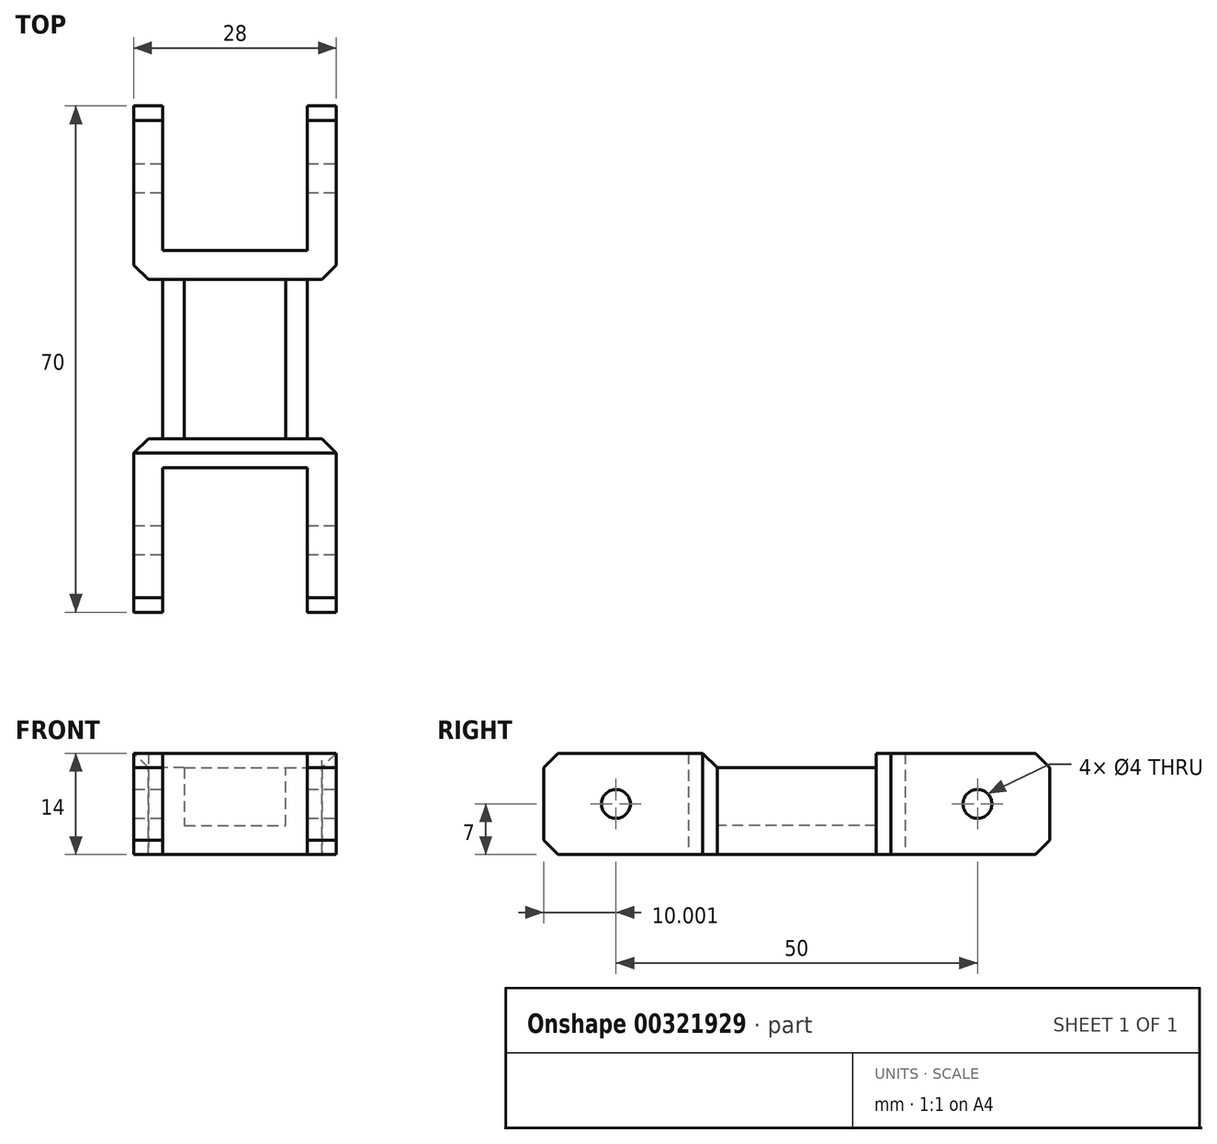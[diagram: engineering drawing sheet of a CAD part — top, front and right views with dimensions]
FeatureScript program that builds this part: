
annotation { "Feature Type Name" : "Feature", "Feature Type Description" : "" }
export const myFeature = defineFeature(function(context is Context, id is Id, definition is map)
    precondition{}
    {
        {
            var Q0;
            Q0=qCreatedBy(makeId("Top.planeOp"),FACE);
            var sketch = newSketch(context, id + "F0", { "sketchPlane" : qUnion([Q0])});
            skLineSegment(sketch, "E0.bottom", {"start": v(-54.4, 33.69) * mm, "end": v(-34.4, 33.69) * mm});
            skLineSegment(sketch, "E0.top", {"start": v(-54.4, 13.29) * mm, "end": v(-34.4, 13.29) * mm});
            skLineSegment(sketch, "E0.left", {"start": v(-54.4, 33.69) * mm, "end": v(-54.4, 13.29) * mm});
            skLineSegment(sketch, "E0.right", {"start": v(-34.4, 33.69) * mm, "end": v(-34.4, 13.29) * mm});
            skLineSegment(sketch, "E1.bottom", {"start": v(-54.4, 63.69) * mm, "end": v(-34.4, 63.69) * mm});
            skLineSegment(sketch, "E1.top", {"start": v(-54.4, 9.29) * mm, "end": v(-34.4, 9.29) * mm});
            skLineSegment(sketch, "E1.left", {"start": v(-54.4, 63.69) * mm, "end": v(-54.4, 9.29) * mm});
            skLineSegment(sketch, "E1.right", {"start": v(-34.4, 63.69) * mm, "end": v(-34.4, 9.29) * mm});
            skLineSegment(sketch, "E2", {"start": v(-54.4, 59.69) * mm, "end": v(-34.4, 59.69) * mm});
            skLineSegment(sketch, "E3", {"start": v(-54.4, 37.69) * mm, "end": v(-34.4, 37.69) * mm});
            skSolve(sketch);
        }
        {
            var Q0;
            {var subQ0=sQuery(id+"F0.wireOp",EDGE,"E2");Q0=makeQuery(id+"F0.imprint","IMPRINT",FACE,{"disambiguationData":[TD([[makeQuery(id+"F0.imprint","IMPRINT",EDGE,{"derivedFrom":subQ0}),-1.0]])]});}
            var Q1;
            {var subQ0=sQuery(id+"F0.wireOp",EDGE,"E1.bottom");Q1=makeQuery(id+"F0.imprint","IMPRINT",FACE,{"disambiguationData":[TD([[makeQuery(id+"F0.imprint","IMPRINT",EDGE,{"derivedFrom":subQ0}),-1.0]])]});}
            var Q2;
            Q2=makeQuery(id+"F0.imprint","IMPRINT",FACE,{"disambiguationData":[TD([[makeQuery(id+"F0.imprint","IMPRINT",EDGE,{"derivedFrom":sQuery(id+"F0.wireOp",EDGE,"E0.bottom")}),1.0]])]});
            var Q3;
            {var subQ0=sQuery(id+"F0.wireOp",EDGE,"E0.bottom");Q3=makeQuery(id+"F0.imprint","IMPRINT",FACE,{"disambiguationData":[TD([[makeQuery(id+"F0.imprint","IMPRINT",EDGE,{"derivedFrom":subQ0}),-1.0]])]});}
            var Q4;
            {var subQ0=sQuery(id+"F0.wireOp",EDGE,"E0.top");Q4=makeQuery(id+"F0.imprint","IMPRINT",FACE,{"disambiguationData":[TD([[makeQuery(id+"F0.imprint","IMPRINT",EDGE,{"derivedFrom":subQ0}),-1.0]])]});}
            extrude(context, id + "F1", {"entities" : qUnion([Q0, Q1, Q2, Q3, Q4]), "oppositeDirection" : true, "depth" : 2 * mm});
        }
        {
            var Q0;
            Q0=makeQuery(id+"F0.imprint","IMPRINT",FACE,{"disambiguationData":[TD([[makeQuery(id+"F0.imprint","IMPRINT",EDGE,{"derivedFrom":sQuery(id+"F0.wireOp",EDGE,"E0.bottom")}),1.0]])]});
            var Q1;
            {var subQ0=sQuery(id+"F0.wireOp",EDGE,"E1.bottom");Q1=makeQuery(id+"F0.imprint","IMPRINT",FACE,{"disambiguationData":[TD([[makeQuery(id+"F0.imprint","IMPRINT",EDGE,{"derivedFrom":subQ0}),-1.0]])]});}
            var Q2;
            {var subQ0=sQuery(id+"F0.wireOp",EDGE,"E0.top");Q2=makeQuery(id+"F0.imprint","IMPRINT",FACE,{"disambiguationData":[TD([[makeQuery(id+"F0.imprint","IMPRINT",EDGE,{"derivedFrom":subQ0}),-1.0]])]});}
            extrude(context, id + "F2", {"entities" : qUnion([Q0, Q1, Q2]), "operationType" : NewBodyOperationType.ADD, "depth" : 10 * mm});
        }
        {
            var Q0;
            {var subQ0=sQuery(id+"F0.wireOp",EDGE,"E1.top");Q0=makeQuery(id+"F2.boolean.opBoolean","MERGE",FACE,{"derivedFrom":[makeQuery(id+"F1.opExtrude","SWEPT_FACE",FACE,{"disambiguationData":[OSD([subQ0])]}),makeQuery(id+"F2.opExtrude","SWEPT_FACE",FACE,{"disambiguationData":[OSD([subQ0])]})]});}
            var sketch = newSketch(context, id + "F3", { "sketchPlane" : qUnion([Q0])});
            skCircle(sketch, "E4", {"center": v(-44.4, 5.5) * mm, "radius": 2.2 * mm});
            skPoint(sketch, "E4.centerSnap0", {"position": v(-44.4, -2) * mm});
            skSolve(sketch);
        }
        {
            var Q0;
            Q0=makeQuery(id+"F3.imprint","IMPRINT",FACE,{"disambiguationData":[TD([[makeQuery(id+"F3.imprint","IMPRINT",EDGE,{"derivedFrom":sQuery(id+"F3.wireOp",EDGE,"E4")}),1.0]])]});
            extrude(context, id + "F4", {"entities" : qUnion([Q0]), "operationType" : NewBodyOperationType.REMOVE, "oppositeDirection" : true, "depth" : 30 * mm, "offsetDistance" : 25 * mm});
        }
        {
            var Q0;
            {var subQ0=sQuery(id+"F0.wireOp",EDGE,"E1.left");Q0=makeQuery(id+"F2.boolean.opBoolean","MERGE",FACE,{"derivedFrom":[makeQuery(id+"F1.opExtrude","SWEPT_FACE",FACE,{"disambiguationData":[OSD([subQ0])]}),makeQuery(id+"F2.opExtrude","SWEPT_FACE",FACE,{"disambiguationData":[OSD([subQ0]),TDD([makeQuery(id+"F0.imprint","IMPRINT",EDGE,{"disambiguationData":[TD([[makeQuery(id+"F0.imprint","INTERSECT",VERTEX,{"derivedFrom":[sQuery(id+"F0.wireOp",EDGE,"E1.bottom"),subQ0]}),-1.0]])],"derivedFrom":subQ0})])]}),makeQuery(id+"F2.opExtrude","SWEPT_FACE",FACE,{"disambiguationData":[OSD([subQ0]),TDD([makeQuery(id+"F0.imprint","IMPRINT",EDGE,{"disambiguationData":[TD([[makeQuery(id+"F0.imprint","INTERSECT",VERTEX,{"derivedFrom":[sQuery(id+"F0.wireOp",EDGE,"E0.bottom"),subQ0]}),1.0]])],"derivedFrom":subQ0})])]}),makeQuery(id+"F2.opExtrude","SWEPT_FACE",FACE,{"disambiguationData":[OSD([subQ0]),TDD([makeQuery(id+"F0.imprint","IMPRINT",EDGE,{"disambiguationData":[TD([[makeQuery(id+"F0.imprint","INTERSECT",VERTEX,{"derivedFrom":[sQuery(id+"F0.wireOp",EDGE,"E0.top"),subQ0]}),-1.0]])],"derivedFrom":subQ0})])]})]});}
            var sketch = newSketch(context, id + "F5", { "sketchPlane" : qUnion([Q0])});
            skLineSegment(sketch, "E5.bottom", {"start": v(-59.69, 10) * mm, "end": v(-83.69, 10) * mm});
            skLineSegment(sketch, "E5.top", {"start": v(-59.69, -2) * mm, "end": v(-83.69, -2) * mm});
            skLineSegment(sketch, "E5.left", {"start": v(-59.69, 10) * mm, "end": v(-59.69, -2) * mm});
            skLineSegment(sketch, "E5.right", {"start": v(-83.69, 10) * mm, "end": v(-83.69, -2) * mm});
            skCircle(sketch, "E6", {"center": v(-73.69, 4) * mm, "radius": 2.6 * mm});
            skPoint(sketch, "E6.centerSnap0", {"position": v(-83.69, 4) * mm});
            skSolve(sketch);
        }
        {
            var Q0;
            {var subQ0=sQuery(id+"F0.wireOp",EDGE,"E1.right");Q0=makeQuery(id+"F2.boolean.opBoolean","MERGE",FACE,{"derivedFrom":[makeQuery(id+"F1.opExtrude","SWEPT_FACE",FACE,{"disambiguationData":[OSD([subQ0])]}),makeQuery(id+"F2.opExtrude","SWEPT_FACE",FACE,{"disambiguationData":[OSD([subQ0]),TDD([makeQuery(id+"F0.imprint","IMPRINT",EDGE,{"disambiguationData":[TD([[makeQuery(id+"F0.imprint","INTERSECT",VERTEX,{"derivedFrom":[sQuery(id+"F0.wireOp",EDGE,"E1.bottom"),subQ0]}),-1.0]])],"derivedFrom":subQ0})])]}),makeQuery(id+"F2.opExtrude","SWEPT_FACE",FACE,{"disambiguationData":[OSD([subQ0]),TDD([makeQuery(id+"F0.imprint","IMPRINT",EDGE,{"disambiguationData":[TD([[makeQuery(id+"F0.imprint","INTERSECT",VERTEX,{"derivedFrom":[sQuery(id+"F0.wireOp",EDGE,"E0.bottom"),subQ0]}),1.0]])],"derivedFrom":subQ0})])]}),makeQuery(id+"F2.opExtrude","SWEPT_FACE",FACE,{"disambiguationData":[OSD([subQ0]),TDD([makeQuery(id+"F0.imprint","IMPRINT",EDGE,{"disambiguationData":[TD([[makeQuery(id+"F0.imprint","INTERSECT",VERTEX,{"derivedFrom":[sQuery(id+"F0.wireOp",EDGE,"E0.top"),subQ0]}),-1.0]])],"derivedFrom":subQ0})])]})]});}
            var sketch = newSketch(context, id + "F6", { "sketchPlane" : qUnion([Q0])});
            skLineSegment(sketch, "E7.bottom", {"start": v(59.69, 10) * mm, "end": v(83.69, 10) * mm});
            skLineSegment(sketch, "E7.top", {"start": v(59.69, -2) * mm, "end": v(83.69, -2) * mm});
            skLineSegment(sketch, "E7.left", {"start": v(59.69, 10) * mm, "end": v(59.69, -2) * mm});
            skLineSegment(sketch, "E7.right", {"start": v(83.69, 10) * mm, "end": v(83.69, -2) * mm});
            skCircle(sketch, "E8", {"center": v(73.69, 4) * mm, "radius": 2.6 * mm});
            skPoint(sketch, "E8.centerSnap0", {"position": v(83.69, 4) * mm});
            skSolve(sketch);
        }
        {
            var Q0;
            {var subQ4=sQuery(id+"F5.wireOp",EDGE,"E5.right");Q0=makeQuery(id+"F5.imprint","IMPRINT",FACE,{"disambiguationData":[TD([[makeQuery(id+"F5.imprint","IMPRINT",EDGE,{"derivedFrom":subQ4}),1.0]])]});}
            var Q1;
            {var subQ3=sQuery(id+"F0.wireOp",EDGE,"E1.left");var subQ5=sQuery(id+"F0.wireOp",EDGE,"E1.bottom");var subQ10=makeQuery(id+"F2.boolean.opBoolean","MERGE",EDGE,{"derivedFrom":[makeQuery(id+"F1.opExtrude","SWEPT_EDGE",EDGE,{"disambiguationData":[OSD([subQ5,subQ3])]}),makeQuery(id+"F2.opExtrude","SWEPT_EDGE",EDGE,{"disambiguationData":[OSD([subQ5,subQ3])]})]});Q1=makeQuery(id+"F5.imprint","IMPRINT",FACE,{"disambiguationData":[TD([[makeQuery(id+"F5.imprint","IMPRINT",EDGE,{"derivedFrom":subQ10}),-1.0]])]});}
            extrude(context, id + "F7", {"entities" : qUnion([Q0, Q1]), "operationType" : NewBodyOperationType.ADD, "depth" : 4 * mm});
        }
        {
            var Q0;
            {var subQ0=sQuery(id+"F5.wireOp",EDGE,"As3iJ9jp-MM02-xgW6-gQvA-6wpTA8jTOXIw.right");Q0=makeQuery(id+"F5.imprint","IMPRINT",FACE,{"disambiguationData":[TD([[makeQuery(id+"F5.imprint","IMPRINT",EDGE,{"derivedFrom":subQ0}),-1.0]])]});}
            var Q1;
            {var subQ5=sQuery(id+"F5.wireOp",EDGE,"D0sxENBk-QWaU-MoL9-KmcH-z9rnvNsLjtkH");Q1=makeQuery(id+"F5.imprint","IMPRINT",FACE,{"disambiguationData":[TD([[makeQuery(id+"F5.imprint","IMPRINT",EDGE,{"derivedFrom":subQ5}),-1.0]])]});}
            var Q2;
            {var subQ4=sQuery(id+"F6.wireOp",EDGE,"E7.right");Q2=makeQuery(id+"F6.imprint","IMPRINT",FACE,{"disambiguationData":[TD([[makeQuery(id+"F6.imprint","IMPRINT",EDGE,{"derivedFrom":subQ4}),-1.0]])]});}
            var Q3;
            {var subQ3=sQuery(id+"F0.wireOp",EDGE,"E1.right");var subQ4=sQuery(id+"F0.wireOp",EDGE,"E1.bottom");var subQ10=makeQuery(id+"F2.boolean.opBoolean","MERGE",EDGE,{"derivedFrom":[makeQuery(id+"F1.opExtrude","SWEPT_EDGE",EDGE,{"disambiguationData":[OSD([subQ4,subQ3])]}),makeQuery(id+"F2.opExtrude","SWEPT_EDGE",EDGE,{"disambiguationData":[OSD([subQ4,subQ3])]})]});Q3=makeQuery(id+"F6.imprint","IMPRINT",FACE,{"disambiguationData":[TD([[makeQuery(id+"F6.imprint","IMPRINT",EDGE,{"derivedFrom":subQ10}),1.0]])]});}
            extrude(context, id + "F8", {"entities" : qUnion([Q0, Q1, Q2, Q3]), "operationType" : NewBodyOperationType.ADD, "depth" : 4 * mm});
        }
        {
            var Q0;
            Q0=makeQuery(id+"F8.boolean.opBoolean","MERGE",FACE,{"derivedFrom":[makeQuery(id+"F7.boolean.opBoolean","MERGE",FACE,{"derivedFrom":[makeQuery(id+"F1.opExtrude","CAP_FACE",FACE,{"disambiguationData":[OSD([sQuery(id+"F0.wireOp",EDGE,"E1.bottom"),sQuery(id+"F0.wireOp",EDGE,"E1.top"),sQuery(id+"F0.wireOp",EDGE,"E1.left"),sQuery(id+"F0.wireOp",EDGE,"E1.right")])],"isStart":false}),makeQuery(id+"F7.opExtrude","SWEPT_FACE",FACE,{"disambiguationData":[OSD([sQuery(id+"F5.wireOp",EDGE,"E5.top")])]})]}),makeQuery(id+"F8.opExtrude","SWEPT_FACE",FACE,{"disambiguationData":[OSD([sQuery(id+"F6.wireOp",EDGE,"E7.top")])]})]});
            var Q1;
            Q1=makeQuery(id+"F8.boolean.opBoolean","MERGE",FACE,{"derivedFrom":[makeQuery(id+"F7.boolean.opBoolean","MERGE",FACE,{"derivedFrom":[makeQuery(id+"F2.opExtrude","CAP_FACE",FACE,{"disambiguationData":[OSD([sQuery(id+"F0.wireOp",EDGE,"E1.bottom"),sQuery(id+"F0.wireOp",EDGE,"E1.left"),sQuery(id+"F0.wireOp",EDGE,"E1.right"),sQuery(id+"F0.wireOp",EDGE,"E2")])],"isStart":false}),makeQuery(id+"F7.opExtrude","SWEPT_FACE",FACE,{"disambiguationData":[OSD([sQuery(id+"F5.wireOp",EDGE,"E5.bottom")])]})]}),makeQuery(id+"F8.opExtrude","SWEPT_FACE",FACE,{"disambiguationData":[OSD([sQuery(id+"F6.wireOp",EDGE,"E7.bottom")])]})]});
            var Q2;
            Q2=makeQuery(id+"F2.opExtrude","CAP_FACE",FACE,{"disambiguationData":[OSD([sQuery(id+"F0.wireOp",EDGE,"E0.bottom"),sQuery(id+"F0.wireOp",EDGE,"E1.left"),sQuery(id+"F0.wireOp",EDGE,"E1.right"),sQuery(id+"F0.wireOp",EDGE,"E3")])],"isStart":false});
            var Q3;
            Q3=makeQuery(id+"F2.opExtrude","CAP_FACE",FACE,{"disambiguationData":[OSD([sQuery(id+"F0.wireOp",EDGE,"E0.top"),sQuery(id+"F0.wireOp",EDGE,"E1.top"),sQuery(id+"F0.wireOp",EDGE,"E1.left"),sQuery(id+"F0.wireOp",EDGE,"E1.right")])],"isStart":false});
            var Q4;
            {var subQ0=sQuery(id+"F0.wireOp",EDGE,"E1.right");var subQ1=sQuery(id+"F0.wireOp",EDGE,"E1.top");Q4=makeQuery(id+"F2.boolean.opBoolean","MERGE",EDGE,{"derivedFrom":[makeQuery(id+"F1.opExtrude","SWEPT_EDGE",EDGE,{"disambiguationData":[OSD([subQ1,subQ0])]}),makeQuery(id+"F2.opExtrude","SWEPT_EDGE",EDGE,{"disambiguationData":[OSD([subQ1,subQ0])]})]});}
            var Q5;
            {var subQ0=sQuery(id+"F0.wireOp",EDGE,"E1.left");var subQ1=sQuery(id+"F0.wireOp",EDGE,"E1.top");Q5=makeQuery(id+"F2.boolean.opBoolean","MERGE",EDGE,{"derivedFrom":[makeQuery(id+"F1.opExtrude","SWEPT_EDGE",EDGE,{"disambiguationData":[OSD([subQ1,subQ0])]}),makeQuery(id+"F2.opExtrude","SWEPT_EDGE",EDGE,{"disambiguationData":[OSD([subQ1,subQ0])]})]});}
            var Q6;
            Q6=makeQuery(id+"F7.opExtrude","CAP_EDGE",EDGE,{"disambiguationData":[OSD([sQuery(id+"F5.wireOp",EDGE,"E5.left")])],"isStart":false});
            var Q7;
            Q7=makeQuery(id+"F8.opExtrude","CAP_EDGE",EDGE,{"disambiguationData":[OSD([sQuery(id+"F6.wireOp",EDGE,"E7.left")])],"isStart":false});
            var Q8;
            Q8=makeQuery(id+"F8.opExtrude","CAP_EDGE",EDGE,{"disambiguationData":[OSD([sQuery(id+"F6.wireOp",EDGE,"E7.right")])],"isStart":false});
            var Q9;
            Q9=makeQuery(id+"F7.opExtrude","CAP_EDGE",EDGE,{"disambiguationData":[OSD([sQuery(id+"F5.wireOp",EDGE,"E5.right")])],"isStart":false});
            fillet(context, id + "F9", {"entities" : qUnion([Q0, Q1, Q2, Q3, Q4, Q5, Q6, Q7, Q8, Q9]), "radius" : 2 * mm, "allowEdgeOverflow" : false});
        }
        {
            var Q0;
            Q0=qCreatedBy(makeId("Top.planeOp"),FACE);
            var sketch = newSketch(context, id + "F10", { "sketchPlane" : qUnion([Q0])});
            skLineSegment(sketch, "E9.bottom", {"start": v(-54.07, -51.84) * mm, "end": v(-34.07, -51.84) * mm});
            skLineSegment(sketch, "E9.top", {"start": v(-54.07, -81.84) * mm, "end": v(-34.07, -81.84) * mm});
            skLineSegment(sketch, "E9.left", {"start": v(-54.07, -51.84) * mm, "end": v(-54.07, -81.84) * mm});
            skLineSegment(sketch, "E9.right", {"start": v(-34.07, -51.84) * mm, "end": v(-34.07, -81.84) * mm});
            skSolve(sketch);
        }
        {
            var Q0;
            Q0=qSketchRegion(id+"F10",true);
            extrude(context, id + "F11", {"entities" : qUnion([Q0]), "depth" : 4 * mm, "offsetDistance" : 25 * mm});
        }
        {
            var Q0;
            Q0=makeQuery(id+"F11.opExtrude","CAP_FACE",FACE,{"disambiguationData":[OSD([sQuery(id+"F10.wireOp",EDGE,"E9.bottom"),sQuery(id+"F10.wireOp",EDGE,"E9.top"),sQuery(id+"F10.wireOp",EDGE,"E9.left"),sQuery(id+"F10.wireOp",EDGE,"E9.right")])],"isStart":false});
            var sketch = newSketch(context, id + "F12", { "sketchPlane" : qUnion([Q0])});
            skLineSegment(sketch, "E10", {"start": v(-54.07, -55.84) * mm, "end": v(-34.07, -55.84) * mm});
            skLineSegment(sketch, "E11", {"start": v(-54.07, -77.84) * mm, "end": v(-34.07, -77.84) * mm});
            skSolve(sketch);
        }
        {
            var Q0;
            {var subQ0=sQuery(id+"F12.wireOp",EDGE,"E10");Q0=makeQuery(id+"F12.imprint","IMPRINT",FACE,{"disambiguationData":[TD([[makeQuery(id+"F12.imprint","IMPRINT",EDGE,{"derivedFrom":subQ0}),1.0]])]});}
            var Q1;
            {var subQ0=sQuery(id+"F12.wireOp",EDGE,"E11");Q1=makeQuery(id+"F12.imprint","IMPRINT",FACE,{"disambiguationData":[TD([[makeQuery(id+"F12.imprint","IMPRINT",EDGE,{"derivedFrom":subQ0}),-1.0]])]});}
            extrude(context, id + "F13", {"entities" : qUnion([Q0, Q1]), "operationType" : NewBodyOperationType.ADD, "depth" : 10 * mm, "offsetDistance" : 25 * mm});
        }
        {
            var Q0;
            {var subQ0=sQuery(id+"F10.wireOp",EDGE,"E9.left");var subQ1=makeQuery(id+"F11.opExtrude","CAP_EDGE",EDGE,{"disambiguationData":[OSD([subQ0])],"isStart":false});Q0=makeQuery(id+"F13.boolean.opBoolean","MERGE",FACE,{"derivedFrom":[makeQuery(id+"F11.opExtrude","SWEPT_FACE",FACE,{"disambiguationData":[OSD([subQ0])]}),makeQuery(id+"F13.opExtrude","SWEPT_FACE",FACE,{"disambiguationData":[OSD([subQ0]),TDD([makeQuery(id+"F12.imprint","IMPRINT",EDGE,{"disambiguationData":[TD([[makeQuery(id+"F12.imprint","INTERSECT",VERTEX,{"derivedFrom":[makeQuery(id+"F11.opExtrude","CAP_EDGE",EDGE,{"disambiguationData":[OSD([sQuery(id+"F10.wireOp",EDGE,"E9.bottom")])],"isStart":false}),subQ1]}),-1.0]])],"derivedFrom":subQ1})])]}),makeQuery(id+"F13.opExtrude","SWEPT_FACE",FACE,{"disambiguationData":[OSD([subQ0]),TDD([makeQuery(id+"F12.imprint","IMPRINT",EDGE,{"disambiguationData":[TD([[makeQuery(id+"F12.imprint","INTERSECT",VERTEX,{"derivedFrom":[makeQuery(id+"F11.opExtrude","CAP_EDGE",EDGE,{"disambiguationData":[OSD([sQuery(id+"F10.wireOp",EDGE,"E9.top")])],"isStart":false}),subQ1]}),1.0]])],"derivedFrom":subQ1})])]})]});}
            var sketch = newSketch(context, id + "F14", { "sketchPlane" : qUnion([Q0])});
            skLineSegment(sketch, "E12", {"start": v(55.84, 4) * mm, "end": v(55.84, 0) * mm});
            skLineSegment(sketch, "E13", {"start": v(77.84, 4) * mm, "end": v(77.84, 0) * mm});
            skSolve(sketch);
        }
        {
            var Q0;
            {var subQ0=sQuery(id+"F10.wireOp",EDGE,"E9.right");var subQ1=makeQuery(id+"F11.opExtrude","CAP_EDGE",EDGE,{"disambiguationData":[OSD([subQ0])],"isStart":false});Q0=makeQuery(id+"F13.boolean.opBoolean","MERGE",FACE,{"derivedFrom":[makeQuery(id+"F11.opExtrude","SWEPT_FACE",FACE,{"disambiguationData":[OSD([subQ0])]}),makeQuery(id+"F13.opExtrude","SWEPT_FACE",FACE,{"disambiguationData":[OSD([subQ0]),TDD([makeQuery(id+"F12.imprint","IMPRINT",EDGE,{"disambiguationData":[TD([[makeQuery(id+"F12.imprint","INTERSECT",VERTEX,{"derivedFrom":[makeQuery(id+"F11.opExtrude","CAP_EDGE",EDGE,{"disambiguationData":[OSD([sQuery(id+"F10.wireOp",EDGE,"E9.bottom")])],"isStart":false}),subQ1]}),-1.0]])],"derivedFrom":subQ1})])]}),makeQuery(id+"F13.opExtrude","SWEPT_FACE",FACE,{"disambiguationData":[OSD([subQ0]),TDD([makeQuery(id+"F12.imprint","IMPRINT",EDGE,{"disambiguationData":[TD([[makeQuery(id+"F12.imprint","INTERSECT",VERTEX,{"derivedFrom":[makeQuery(id+"F11.opExtrude","CAP_EDGE",EDGE,{"disambiguationData":[OSD([sQuery(id+"F10.wireOp",EDGE,"E9.top")])],"isStart":false}),subQ1]}),1.0]])],"derivedFrom":subQ1})])]})]});}
            var sketch = newSketch(context, id + "F15", { "sketchPlane" : qUnion([Q0])});
            skLineSegment(sketch, "E14", {"start": v(-77.84, 4) * mm, "end": v(-77.84, 0) * mm});
            skLineSegment(sketch, "E15", {"start": v(-55.84, 4) * mm, "end": v(-55.84, 0) * mm});
            skSolve(sketch);
        }
        {
            var Q0;
            {var subQ5=sQuery(id+"F15.wireOp",EDGE,"E14");Q0=makeQuery(id+"F15.imprint","IMPRINT",FACE,{"disambiguationData":[TD([[makeQuery(id+"F15.imprint","IMPRINT",EDGE,{"derivedFrom":subQ5}),-1.0]])]});}
            var Q1;
            {var subQ5=sQuery(id+"F15.wireOp",EDGE,"E15");Q1=makeQuery(id+"F15.imprint","IMPRINT",FACE,{"disambiguationData":[TD([[makeQuery(id+"F15.imprint","IMPRINT",EDGE,{"derivedFrom":subQ5}),1.0]])]});}
            extrude(context, id + "F16", {"entities" : qUnion([Q0, Q1]), "operationType" : NewBodyOperationType.ADD, "depth" : 4 * mm, "offsetDistance" : 25 * mm});
        }
        {
            var Q0;
            {var subQ5=sQuery(id+"F14.wireOp",EDGE,"E12");Q0=makeQuery(id+"F14.imprint","IMPRINT",FACE,{"disambiguationData":[TD([[makeQuery(id+"F14.imprint","IMPRINT",EDGE,{"derivedFrom":subQ5}),-1.0]])]});}
            var Q1;
            {var subQ5=sQuery(id+"F14.wireOp",EDGE,"E13");Q1=makeQuery(id+"F14.imprint","IMPRINT",FACE,{"disambiguationData":[TD([[makeQuery(id+"F14.imprint","IMPRINT",EDGE,{"derivedFrom":subQ5}),1.0]])]});}
            extrude(context, id + "F17", {"entities" : qUnion([Q0, Q1]), "operationType" : NewBodyOperationType.ADD, "depth" : 4 * mm, "offsetDistance" : 25 * mm});
        }
        {
            var Q0;
            {var subQ0=sQuery(id+"F10.wireOp",EDGE,"E9.bottom");Q0=makeQuery(id+"F17.boolean.opBoolean","MERGE",FACE,{"derivedFrom":[makeQuery(id+"F16.boolean.opBoolean","MERGE",FACE,{"derivedFrom":[makeQuery(id+"F13.boolean.opBoolean","MERGE",FACE,{"derivedFrom":[makeQuery(id+"F11.opExtrude","SWEPT_FACE",FACE,{"disambiguationData":[OSD([subQ0])]}),makeQuery(id+"F13.opExtrude","SWEPT_FACE",FACE,{"disambiguationData":[OSD([subQ0])]})]}),makeQuery(id+"F16.opExtrude","SWEPT_FACE",FACE,{"disambiguationData":[OSD([subQ0,sQuery(id+"F10.wireOp",EDGE,"E9.right")])]})]}),makeQuery(id+"F17.opExtrude","SWEPT_FACE",FACE,{"disambiguationData":[OSD([subQ0,sQuery(id+"F10.wireOp",EDGE,"E9.left")])]})]});}
            var sketch = newSketch(context, id + "F18", { "sketchPlane" : qUnion([Q0])});
            skLineSegment(sketch, "E16", {"start": v(34.07, 14) * mm, "end": v(34.07, 0) * mm});
            skLineSegment(sketch, "E17", {"start": v(54.07, 14) * mm, "end": v(54.07, 0) * mm});
            skSolve(sketch);
        }
        {
            var Q0;
            {var subQ0=sQuery(id+"F10.wireOp",EDGE,"E9.top");Q0=makeQuery(id+"F17.boolean.opBoolean","MERGE",FACE,{"derivedFrom":[makeQuery(id+"F16.boolean.opBoolean","MERGE",FACE,{"derivedFrom":[makeQuery(id+"F13.boolean.opBoolean","MERGE",FACE,{"derivedFrom":[makeQuery(id+"F11.opExtrude","SWEPT_FACE",FACE,{"disambiguationData":[OSD([subQ0])]}),makeQuery(id+"F13.opExtrude","SWEPT_FACE",FACE,{"disambiguationData":[OSD([subQ0])]})]}),makeQuery(id+"F16.opExtrude","SWEPT_FACE",FACE,{"disambiguationData":[OSD([subQ0,sQuery(id+"F10.wireOp",EDGE,"E9.right")])]})]}),makeQuery(id+"F17.opExtrude","SWEPT_FACE",FACE,{"disambiguationData":[OSD([subQ0,sQuery(id+"F10.wireOp",EDGE,"E9.left")])]})]});}
            var sketch = newSketch(context, id + "F19", { "sketchPlane" : qUnion([Q0])});
            skLineSegment(sketch, "E18", {"start": v(-54.07, 14) * mm, "end": v(-54.07, 0) * mm});
            skLineSegment(sketch, "E19", {"start": v(-34.07, 14) * mm, "end": v(-34.07, 0) * mm});
            skSolve(sketch);
        }
        {
            var Q0;
            {var subQ0=sQuery(id+"F19.wireOp",EDGE,"E18");Q0=makeQuery(id+"F19.imprint","IMPRINT",FACE,{"disambiguationData":[TD([[makeQuery(id+"F19.imprint","IMPRINT",EDGE,{"derivedFrom":subQ0}),-1.0]])]});}
            var Q1;
            {var subQ0=sQuery(id+"F19.wireOp",EDGE,"E19");Q1=makeQuery(id+"F19.imprint","IMPRINT",FACE,{"disambiguationData":[TD([[makeQuery(id+"F19.imprint","IMPRINT",EDGE,{"derivedFrom":subQ0}),1.0]])]});}
            extrude(context, id + "F20", {"entities" : qUnion([Q0, Q1]), "operationType" : NewBodyOperationType.ADD, "depth" : 20 * mm, "offsetDistance" : 25 * mm});
        }
        {
            var Q0;
            {var subQ0=sQuery(id+"F18.wireOp",EDGE,"E16");Q0=makeQuery(id+"F18.imprint","IMPRINT",FACE,{"disambiguationData":[TD([[makeQuery(id+"F18.imprint","IMPRINT",EDGE,{"derivedFrom":subQ0}),-1.0]])]});}
            var Q1;
            {var subQ0=sQuery(id+"F18.wireOp",EDGE,"E17");Q1=makeQuery(id+"F18.imprint","IMPRINT",FACE,{"disambiguationData":[TD([[makeQuery(id+"F18.imprint","IMPRINT",EDGE,{"derivedFrom":subQ0}),1.0]])]});}
            extrude(context, id + "F21", {"entities" : qUnion([Q0, Q1]), "operationType" : NewBodyOperationType.ADD, "depth" : 20 * mm, "offsetDistance" : 25 * mm});
        }
        {
            var Q0;
            {var subQ0=sQuery(id+"F10.wireOp",EDGE,"E9.left");var subQ1=makeQuery(id+"F11.opExtrude","CAP_EDGE",EDGE,{"disambiguationData":[OSD([subQ0])],"isStart":false});Q0=makeQuery(id+"F13.boolean.opBoolean","MERGE",FACE,{"derivedFrom":[makeQuery(id+"F11.opExtrude","SWEPT_FACE",FACE,{"disambiguationData":[OSD([subQ0])]}),makeQuery(id+"F13.opExtrude","SWEPT_FACE",FACE,{"disambiguationData":[OSD([subQ0]),TDD([makeQuery(id+"F12.imprint","IMPRINT",EDGE,{"disambiguationData":[TD([[makeQuery(id+"F12.imprint","INTERSECT",VERTEX,{"derivedFrom":[makeQuery(id+"F11.opExtrude","CAP_EDGE",EDGE,{"disambiguationData":[OSD([sQuery(id+"F10.wireOp",EDGE,"E9.bottom")])],"isStart":false}),subQ1]}),-1.0]])],"derivedFrom":subQ1})])]}),makeQuery(id+"F13.opExtrude","SWEPT_FACE",FACE,{"disambiguationData":[OSD([subQ0]),TDD([makeQuery(id+"F12.imprint","IMPRINT",EDGE,{"disambiguationData":[TD([[makeQuery(id+"F12.imprint","INTERSECT",VERTEX,{"derivedFrom":[makeQuery(id+"F11.opExtrude","CAP_EDGE",EDGE,{"disambiguationData":[OSD([sQuery(id+"F10.wireOp",EDGE,"E9.top")])],"isStart":false}),subQ1]}),1.0]])],"derivedFrom":subQ1})])]})]});}
            var sketch = newSketch(context, id + "F22", { "sketchPlane" : qUnion([Q0])});
            skLineSegment(sketch, "E20", {"start": v(55.84, 4) * mm, "end": v(55.84, 12) * mm});
            skLineSegment(sketch, "E21", {"start": v(55.84, 12) * mm, "end": v(77.84, 12) * mm});
            skLineSegment(sketch, "E22", {"start": v(77.84, 12) * mm, "end": v(77.84, 4) * mm});
            skLineSegment(sketch, "E23", {"start": v(77.84, 4) * mm, "end": v(55.84, 4) * mm});
            skSolve(sketch);
        }
        {
            var Q0;
            Q0=makeQuery(id+"F22.imprint","IMPRINT",FACE,{"disambiguationData":[TD([[makeQuery(id+"F22.imprint","IMPRINT",EDGE,{"derivedFrom":sQuery(id+"F22.wireOp",EDGE,"E20")}),-1.0]])]});
            extrude(context, id + "F23", {"entities" : qUnion([Q0]), "operationType" : NewBodyOperationType.ADD, "oppositeDirection" : true, "depth" : 3 * mm, "offsetDistance" : 25 * mm});
        }
        {
            var Q0;
            {var subQ0=sQuery(id+"F10.wireOp",EDGE,"E9.right");var subQ1=makeQuery(id+"F11.opExtrude","CAP_EDGE",EDGE,{"disambiguationData":[OSD([subQ0])],"isStart":false});Q0=makeQuery(id+"F13.boolean.opBoolean","MERGE",FACE,{"derivedFrom":[makeQuery(id+"F11.opExtrude","SWEPT_FACE",FACE,{"disambiguationData":[OSD([subQ0])]}),makeQuery(id+"F13.opExtrude","SWEPT_FACE",FACE,{"disambiguationData":[OSD([subQ0]),TDD([makeQuery(id+"F12.imprint","IMPRINT",EDGE,{"disambiguationData":[TD([[makeQuery(id+"F12.imprint","INTERSECT",VERTEX,{"derivedFrom":[makeQuery(id+"F11.opExtrude","CAP_EDGE",EDGE,{"disambiguationData":[OSD([sQuery(id+"F10.wireOp",EDGE,"E9.bottom")])],"isStart":false}),subQ1]}),-1.0]])],"derivedFrom":subQ1})])]}),makeQuery(id+"F13.opExtrude","SWEPT_FACE",FACE,{"disambiguationData":[OSD([subQ0]),TDD([makeQuery(id+"F12.imprint","IMPRINT",EDGE,{"disambiguationData":[TD([[makeQuery(id+"F12.imprint","INTERSECT",VERTEX,{"derivedFrom":[makeQuery(id+"F11.opExtrude","CAP_EDGE",EDGE,{"disambiguationData":[OSD([sQuery(id+"F10.wireOp",EDGE,"E9.top")])],"isStart":false}),subQ1]}),1.0]])],"derivedFrom":subQ1})])]})]});}
            var sketch = newSketch(context, id + "F24", { "sketchPlane" : qUnion([Q0])});
            skLineSegment(sketch, "E24", {"start": v(-77.84, 4) * mm, "end": v(-77.84, 12) * mm});
            skLineSegment(sketch, "E25", {"start": v(-77.84, 12) * mm, "end": v(-55.84, 12) * mm});
            skLineSegment(sketch, "E26", {"start": v(-55.84, 12) * mm, "end": v(-55.84, 4) * mm});
            skLineSegment(sketch, "E27", {"start": v(-55.84, 4) * mm, "end": v(-77.84, 4) * mm});
            skSolve(sketch);
        }
        {
            var Q0;
            Q0=makeQuery(id+"F24.imprint","IMPRINT",FACE,{"disambiguationData":[TD([[makeQuery(id+"F24.imprint","IMPRINT",EDGE,{"derivedFrom":sQuery(id+"F24.wireOp",EDGE,"E24")}),-1.0]])]});
            extrude(context, id + "F25", {"entities" : qUnion([Q0]), "operationType" : NewBodyOperationType.ADD, "oppositeDirection" : true, "depth" : 3 * mm, "offsetDistance" : 25 * mm});
        }
        {
            var Q0;
            {var subQ0=sQuery(id+"F10.wireOp",EDGE,"E9.right");var subQ1=sQuery(id+"F10.wireOp",EDGE,"E9.top");Q0=makeQuery(id+"F20.boolean.opBoolean","MERGE",FACE,{"derivedFrom":[makeQuery(id+"F16.opExtrude","CAP_FACE",FACE,{"disambiguationData":[OSD([subQ1,subQ0,sQuery(id+"F12.wireOp",EDGE,"E11"),sQuery(id+"F15.wireOp",EDGE,"E14")])],"isStart":false}),makeQuery(id+"F20.opExtrude","SWEPT_FACE",FACE,{"disambiguationData":[OSD([subQ1,subQ0])]})]});}
            var sketch = newSketch(context, id + "F26", { "sketchPlane" : qUnion([Q0])});
            skCircle(sketch, "E28", {"center": v(-91.84, 7) * mm, "radius": 2 * mm});
            skPoint(sketch, "E28.centerSnap0", {"position": v(-101.84, 7) * mm});
            skPoint(sketch, "E28.centerSnap1", {"position": v(-89.84, 14) * mm});
            skSolve(sketch);
        }
        {
            var Q0;
            {var subQ0=sQuery(id+"F10.wireOp",EDGE,"E9.right");var subQ1=sQuery(id+"F10.wireOp",EDGE,"E9.bottom");Q0=makeQuery(id+"F21.boolean.opBoolean","MERGE",FACE,{"derivedFrom":[makeQuery(id+"F16.opExtrude","CAP_FACE",FACE,{"disambiguationData":[OSD([subQ1,subQ0,sQuery(id+"F12.wireOp",EDGE,"E10"),sQuery(id+"F15.wireOp",EDGE,"E15")])],"isStart":false}),makeQuery(id+"F21.opExtrude","SWEPT_FACE",FACE,{"disambiguationData":[OSD([subQ1,subQ0])]})]});}
            var sketch = newSketch(context, id + "F27", { "sketchPlane" : qUnion([Q0])});
            skCircle(sketch, "E29", {"center": v(-41.84, 7) * mm, "radius": 2 * mm});
            skPoint(sketch, "E29.centerSnap0", {"position": v(-31.84, 7) * mm});
            skPoint(sketch, "E29.centerSnap1", {"position": v(-43.84, 14) * mm});
            skSolve(sketch);
        }
        {
            var Q0;
            Q0=makeQuery(id+"F26.imprint","IMPRINT",FACE,{"disambiguationData":[TD([[makeQuery(id+"F26.imprint","IMPRINT",EDGE,{"derivedFrom":sQuery(id+"F26.wireOp",EDGE,"E28")}),1.0]])]});
            var Q1;
            Q1=makeQuery(id+"F27.imprint","IMPRINT",FACE,{"disambiguationData":[TD([[makeQuery(id+"F27.imprint","IMPRINT",EDGE,{"derivedFrom":sQuery(id+"F27.wireOp",EDGE,"E29")}),1.0]])]});
            extrude(context, id + "F28", {"entities" : qUnion([Q0, Q1]), "operationType" : NewBodyOperationType.REMOVE, "endBound" : BoundingType.THROUGH_ALL, "oppositeDirection" : true, "depth" : 25 * mm, "offsetDistance" : 25 * mm});
        }
        {
            var Q0;
            {var subQ0=sQuery(id+"F10.wireOp",EDGE,"E9.left");var subQ1=sQuery(id+"F10.wireOp",EDGE,"E9.top");var subQ2=sQuery(id+"F10.wireOp",EDGE,"E9.right");var subQ3=makeQuery(id+"F17.boolean.opBoolean","MERGE",EDGE,{"derivedFrom":[makeQuery(id+"F16.boolean.opBoolean","MERGE",EDGE,{"derivedFrom":[makeQuery(id+"F11.opExtrude","CAP_EDGE",EDGE,{"disambiguationData":[OSD([subQ1])],"isStart":true}),makeQuery(id+"F16.opExtrude","SWEPT_EDGE",EDGE,{"disambiguationData":[OSD([subQ1,subQ2]),TDD([makeQuery(id+"F15.imprint","INTERSECT",VERTEX,{"derivedFrom":[makeQuery(id+"F11.opExtrude","CAP_EDGE",EDGE,{"disambiguationData":[OSD([subQ2])],"isStart":true}),makeQuery(id+"F13.boolean.opBoolean","MERGE",EDGE,{"derivedFrom":[makeQuery(id+"F11.opExtrude","SWEPT_EDGE",EDGE,{"disambiguationData":[OSD([subQ1,subQ2])]}),makeQuery(id+"F13.opExtrude","SWEPT_EDGE",EDGE,{"disambiguationData":[OSD([subQ1,subQ2])]})]})]})])]})]}),makeQuery(id+"F17.opExtrude","SWEPT_EDGE",EDGE,{"disambiguationData":[OSD([subQ1,subQ0]),TDD([makeQuery(id+"F14.imprint","INTERSECT",VERTEX,{"derivedFrom":[makeQuery(id+"F11.opExtrude","CAP_EDGE",EDGE,{"disambiguationData":[OSD([subQ0])],"isStart":true}),makeQuery(id+"F13.boolean.opBoolean","MERGE",EDGE,{"derivedFrom":[makeQuery(id+"F11.opExtrude","SWEPT_EDGE",EDGE,{"disambiguationData":[OSD([subQ1,subQ0])]}),makeQuery(id+"F13.opExtrude","SWEPT_EDGE",EDGE,{"disambiguationData":[OSD([subQ1,subQ0])]})]})]})])]})]});Q0=makeQuery(id+"F20.opExtrude","CAP_EDGE",EDGE,{"disambiguationData":[OSD([subQ1,subQ0,subQ2]),TDD([makeQuery(id+"F19.imprint","IMPRINT",EDGE,{"disambiguationData":[TD([[makeQuery(id+"F19.imprint","INTERSECT",VERTEX,{"derivedFrom":[subQ3,sQuery(id+"F19.wireOp",EDGE,"E19")]}),-1.0]])],"derivedFrom":subQ3})])],"isStart":false});}
            var Q1;
            Q1=makeQuery(id+"F16.opExtrude","CAP_EDGE",EDGE,{"disambiguationData":[OSD([sQuery(id+"F10.wireOp",EDGE,"E9.right"),sQuery(id+"F12.wireOp",EDGE,"E11"),sQuery(id+"F15.wireOp",EDGE,"E14")])],"isStart":false});
            var Q2;
            {var subQ0=sQuery(id+"F12.wireOp",EDGE,"E11");Q2=makeQuery(id+"F17.boolean.opBoolean","MERGE",EDGE,{"derivedFrom":[makeQuery(id+"F16.boolean.opBoolean","MERGE",EDGE,{"derivedFrom":[makeQuery(id+"F13.opExtrude","CAP_EDGE",EDGE,{"disambiguationData":[OSD([subQ0])],"isStart":false}),makeQuery(id+"F16.opExtrude","SWEPT_EDGE",EDGE,{"disambiguationData":[OSD([sQuery(id+"F10.wireOp",EDGE,"E9.right"),subQ0])]})]}),makeQuery(id+"F17.opExtrude","SWEPT_EDGE",EDGE,{"disambiguationData":[OSD([sQuery(id+"F10.wireOp",EDGE,"E9.left"),subQ0])]})]});}
            var Q3;
            Q3=makeQuery(id+"F17.opExtrude","CAP_EDGE",EDGE,{"disambiguationData":[OSD([sQuery(id+"F10.wireOp",EDGE,"E9.left"),sQuery(id+"F12.wireOp",EDGE,"E11"),sQuery(id+"F14.wireOp",EDGE,"E13")])],"isStart":false});
            var Q4;
            Q4=makeQuery(id+"F13.opExtrude","CAP_EDGE",EDGE,{"disambiguationData":[OSD([sQuery(id+"F12.wireOp",EDGE,"E11")])],"isStart":true});
            var Q5;
            Q5=makeQuery(id+"F13.opExtrude","CAP_EDGE",EDGE,{"disambiguationData":[OSD([sQuery(id+"F12.wireOp",EDGE,"E10")])],"isStart":true});
            var Q6;
            Q6=makeQuery(id+"F23.opExtrude","CAP_EDGE",EDGE,{"disambiguationData":[OSD([sQuery(id+"F22.wireOp",EDGE,"E20")])],"isStart":false});
            var Q7;
            Q7=makeQuery(id+"F25.opExtrude","CAP_EDGE",EDGE,{"disambiguationData":[OSD([sQuery(id+"F24.wireOp",EDGE,"E26")])],"isStart":false});
            var Q8;
            Q8=makeQuery(id+"F25.boolean.opBoolean","MERGE",EDGE,{"derivedFrom":[makeQuery(id+"F16.opExtrude","CAP_EDGE",EDGE,{"disambiguationData":[OSD([sQuery(id+"F10.wireOp",EDGE,"E9.right"),sQuery(id+"F12.wireOp",EDGE,"E10"),sQuery(id+"F15.wireOp",EDGE,"E15")])],"isStart":true}),makeQuery(id+"F25.opExtrude","CAP_EDGE",EDGE,{"disambiguationData":[OSD([sQuery(id+"F24.wireOp",EDGE,"E26")])],"isStart":true})]});
            var Q9;
            Q9=makeQuery(id+"F25.opExtrude","SWEPT_EDGE",EDGE,{"disambiguationData":[OSD([sQuery(id+"F24.wireOp",EDGE,"E25"),sQuery(id+"F24.wireOp",EDGE,"E26")])]});
            var Q10;
            Q10=makeQuery(id+"F23.opExtrude","SWEPT_EDGE",EDGE,{"disambiguationData":[OSD([sQuery(id+"F22.wireOp",EDGE,"E20"),sQuery(id+"F22.wireOp",EDGE,"E21")])]});
            var Q11;
            Q11=makeQuery(id+"F23.boolean.opBoolean","MERGE",EDGE,{"derivedFrom":[makeQuery(id+"F17.opExtrude","CAP_EDGE",EDGE,{"disambiguationData":[OSD([sQuery(id+"F10.wireOp",EDGE,"E9.left"),sQuery(id+"F12.wireOp",EDGE,"E10"),sQuery(id+"F14.wireOp",EDGE,"E12")])],"isStart":true}),makeQuery(id+"F23.opExtrude","CAP_EDGE",EDGE,{"disambiguationData":[OSD([sQuery(id+"F22.wireOp",EDGE,"E20")])],"isStart":true})]});
            var Q12;
            Q12=makeQuery(id+"F16.opExtrude","CAP_EDGE",EDGE,{"disambiguationData":[OSD([sQuery(id+"F10.wireOp",EDGE,"E9.right"),sQuery(id+"F12.wireOp",EDGE,"E10"),sQuery(id+"F15.wireOp",EDGE,"E15")])],"isStart":false});
            var Q13;
            Q13=makeQuery(id+"F17.opExtrude","CAP_EDGE",EDGE,{"disambiguationData":[OSD([sQuery(id+"F10.wireOp",EDGE,"E9.left"),sQuery(id+"F12.wireOp",EDGE,"E10"),sQuery(id+"F14.wireOp",EDGE,"E12")])],"isStart":false});
            var Q14;
            {var subQ0=sQuery(id+"F10.wireOp",EDGE,"E9.left");var subQ1=sQuery(id+"F10.wireOp",EDGE,"E9.bottom");var subQ2=makeQuery(id+"F11.opExtrude","CAP_EDGE",EDGE,{"disambiguationData":[OSD([subQ0])],"isStart":false});var subQ3=makeQuery(id+"F11.opExtrude","CAP_EDGE",EDGE,{"disambiguationData":[OSD([subQ1])],"isStart":false});var subQ5=sQuery(id+"F10.wireOp",EDGE,"E9.right");var subQ6=makeQuery(id+"F11.opExtrude","CAP_EDGE",EDGE,{"disambiguationData":[OSD([subQ5])],"isStart":false});var subQ7=makeQuery(id+"F17.boolean.opBoolean","MERGE",EDGE,{"derivedFrom":[makeQuery(id+"F16.boolean.opBoolean","MERGE",EDGE,{"derivedFrom":[makeQuery(id+"F13.opExtrude","CAP_EDGE",EDGE,{"disambiguationData":[OSD([subQ1])],"isStart":false}),makeQuery(id+"F16.opExtrude","SWEPT_EDGE",EDGE,{"disambiguationData":[OSD([subQ1,subQ5]),TDD([makeQuery(id+"F15.imprint","INTERSECT",VERTEX,{"derivedFrom":[makeQuery(id+"F13.opExtrude","CAP_EDGE",EDGE,{"disambiguationData":[OSD([subQ5]),TDD([makeQuery(id+"F12.imprint","IMPRINT",EDGE,{"disambiguationData":[TD([[makeQuery(id+"F12.imprint","INTERSECT",VERTEX,{"derivedFrom":[subQ3,subQ6]}),-1.0]])],"derivedFrom":subQ6})])],"isStart":false}),makeQuery(id+"F13.boolean.opBoolean","MERGE",EDGE,{"derivedFrom":[makeQuery(id+"F11.opExtrude","SWEPT_EDGE",EDGE,{"disambiguationData":[OSD([subQ1,subQ5])]}),makeQuery(id+"F13.opExtrude","SWEPT_EDGE",EDGE,{"disambiguationData":[OSD([subQ1,subQ5])]})]})]})])]})]}),makeQuery(id+"F17.opExtrude","SWEPT_EDGE",EDGE,{"disambiguationData":[OSD([subQ1,subQ0]),TDD([makeQuery(id+"F14.imprint","INTERSECT",VERTEX,{"derivedFrom":[makeQuery(id+"F13.opExtrude","CAP_EDGE",EDGE,{"disambiguationData":[OSD([subQ0]),TDD([makeQuery(id+"F12.imprint","IMPRINT",EDGE,{"disambiguationData":[TD([[makeQuery(id+"F12.imprint","INTERSECT",VERTEX,{"derivedFrom":[subQ3,subQ2]}),-1.0]])],"derivedFrom":subQ2})])],"isStart":false}),makeQuery(id+"F13.boolean.opBoolean","MERGE",EDGE,{"derivedFrom":[makeQuery(id+"F11.opExtrude","SWEPT_EDGE",EDGE,{"disambiguationData":[OSD([subQ1,subQ0])]}),makeQuery(id+"F13.opExtrude","SWEPT_EDGE",EDGE,{"disambiguationData":[OSD([subQ1,subQ0])]})]})]})])]})]});Q14=makeQuery(id+"F21.opExtrude","CAP_EDGE",EDGE,{"disambiguationData":[OSD([subQ1,subQ0,subQ5]),TDD([makeQuery(id+"F18.imprint","IMPRINT",EDGE,{"disambiguationData":[TD([[makeQuery(id+"F18.imprint","INTERSECT",VERTEX,{"derivedFrom":[subQ7,sQuery(id+"F18.wireOp",EDGE,"E16")]}),-1.0]])],"derivedFrom":subQ7})])],"isStart":false});}
            var Q15;
            {var subQ0=sQuery(id+"F10.wireOp",EDGE,"E9.left");var subQ1=sQuery(id+"F10.wireOp",EDGE,"E9.bottom");var subQ2=makeQuery(id+"F11.opExtrude","CAP_EDGE",EDGE,{"disambiguationData":[OSD([subQ0])],"isStart":false});var subQ3=makeQuery(id+"F11.opExtrude","CAP_EDGE",EDGE,{"disambiguationData":[OSD([subQ1])],"isStart":false});var subQ5=sQuery(id+"F10.wireOp",EDGE,"E9.right");var subQ6=makeQuery(id+"F11.opExtrude","CAP_EDGE",EDGE,{"disambiguationData":[OSD([subQ5])],"isStart":false});var subQ7=makeQuery(id+"F17.boolean.opBoolean","MERGE",EDGE,{"derivedFrom":[makeQuery(id+"F16.boolean.opBoolean","MERGE",EDGE,{"derivedFrom":[makeQuery(id+"F13.opExtrude","CAP_EDGE",EDGE,{"disambiguationData":[OSD([subQ1])],"isStart":false}),makeQuery(id+"F16.opExtrude","SWEPT_EDGE",EDGE,{"disambiguationData":[OSD([subQ1,subQ5]),TDD([makeQuery(id+"F15.imprint","INTERSECT",VERTEX,{"derivedFrom":[makeQuery(id+"F13.opExtrude","CAP_EDGE",EDGE,{"disambiguationData":[OSD([subQ5]),TDD([makeQuery(id+"F12.imprint","IMPRINT",EDGE,{"disambiguationData":[TD([[makeQuery(id+"F12.imprint","INTERSECT",VERTEX,{"derivedFrom":[subQ3,subQ6]}),-1.0]])],"derivedFrom":subQ6})])],"isStart":false}),makeQuery(id+"F13.boolean.opBoolean","MERGE",EDGE,{"derivedFrom":[makeQuery(id+"F11.opExtrude","SWEPT_EDGE",EDGE,{"disambiguationData":[OSD([subQ1,subQ5])]}),makeQuery(id+"F13.opExtrude","SWEPT_EDGE",EDGE,{"disambiguationData":[OSD([subQ1,subQ5])]})]})]})])]})]}),makeQuery(id+"F17.opExtrude","SWEPT_EDGE",EDGE,{"disambiguationData":[OSD([subQ1,subQ0]),TDD([makeQuery(id+"F14.imprint","INTERSECT",VERTEX,{"derivedFrom":[makeQuery(id+"F13.opExtrude","CAP_EDGE",EDGE,{"disambiguationData":[OSD([subQ0]),TDD([makeQuery(id+"F12.imprint","IMPRINT",EDGE,{"disambiguationData":[TD([[makeQuery(id+"F12.imprint","INTERSECT",VERTEX,{"derivedFrom":[subQ3,subQ2]}),-1.0]])],"derivedFrom":subQ2})])],"isStart":false}),makeQuery(id+"F13.boolean.opBoolean","MERGE",EDGE,{"derivedFrom":[makeQuery(id+"F11.opExtrude","SWEPT_EDGE",EDGE,{"disambiguationData":[OSD([subQ1,subQ0])]}),makeQuery(id+"F13.opExtrude","SWEPT_EDGE",EDGE,{"disambiguationData":[OSD([subQ1,subQ0])]})]})]})])]})]});Q15=makeQuery(id+"F21.opExtrude","CAP_EDGE",EDGE,{"disambiguationData":[OSD([subQ1,subQ0,subQ5]),TDD([makeQuery(id+"F18.imprint","IMPRINT",EDGE,{"disambiguationData":[TD([[makeQuery(id+"F18.imprint","INTERSECT",VERTEX,{"derivedFrom":[subQ7,sQuery(id+"F18.wireOp",EDGE,"E17")]}),1.0]])],"derivedFrom":subQ7})])],"isStart":false});}
            var Q16;
            {var subQ0=sQuery(id+"F10.wireOp",EDGE,"E9.left");var subQ1=sQuery(id+"F10.wireOp",EDGE,"E9.bottom");var subQ2=sQuery(id+"F10.wireOp",EDGE,"E9.right");var subQ3=makeQuery(id+"F17.boolean.opBoolean","MERGE",EDGE,{"derivedFrom":[makeQuery(id+"F16.boolean.opBoolean","MERGE",EDGE,{"derivedFrom":[makeQuery(id+"F11.opExtrude","CAP_EDGE",EDGE,{"disambiguationData":[OSD([subQ1])],"isStart":true}),makeQuery(id+"F16.opExtrude","SWEPT_EDGE",EDGE,{"disambiguationData":[OSD([subQ1,subQ2]),TDD([makeQuery(id+"F15.imprint","INTERSECT",VERTEX,{"derivedFrom":[makeQuery(id+"F11.opExtrude","CAP_EDGE",EDGE,{"disambiguationData":[OSD([subQ2])],"isStart":true}),makeQuery(id+"F13.boolean.opBoolean","MERGE",EDGE,{"derivedFrom":[makeQuery(id+"F11.opExtrude","SWEPT_EDGE",EDGE,{"disambiguationData":[OSD([subQ1,subQ2])]}),makeQuery(id+"F13.opExtrude","SWEPT_EDGE",EDGE,{"disambiguationData":[OSD([subQ1,subQ2])]})]})]})])]})]}),makeQuery(id+"F17.opExtrude","SWEPT_EDGE",EDGE,{"disambiguationData":[OSD([subQ1,subQ0]),TDD([makeQuery(id+"F14.imprint","INTERSECT",VERTEX,{"derivedFrom":[makeQuery(id+"F11.opExtrude","CAP_EDGE",EDGE,{"disambiguationData":[OSD([subQ0])],"isStart":true}),makeQuery(id+"F13.boolean.opBoolean","MERGE",EDGE,{"derivedFrom":[makeQuery(id+"F11.opExtrude","SWEPT_EDGE",EDGE,{"disambiguationData":[OSD([subQ1,subQ0])]}),makeQuery(id+"F13.opExtrude","SWEPT_EDGE",EDGE,{"disambiguationData":[OSD([subQ1,subQ0])]})]})]})])]})]});Q16=makeQuery(id+"F21.opExtrude","CAP_EDGE",EDGE,{"disambiguationData":[OSD([subQ1,subQ0,subQ2]),TDD([makeQuery(id+"F18.imprint","IMPRINT",EDGE,{"disambiguationData":[TD([[makeQuery(id+"F18.imprint","INTERSECT",VERTEX,{"derivedFrom":[subQ3,sQuery(id+"F18.wireOp",EDGE,"E17")]}),1.0]])],"derivedFrom":subQ3})])],"isStart":false});}
            var Q17;
            {var subQ0=sQuery(id+"F10.wireOp",EDGE,"E9.left");var subQ1=sQuery(id+"F10.wireOp",EDGE,"E9.bottom");var subQ2=sQuery(id+"F10.wireOp",EDGE,"E9.right");var subQ3=makeQuery(id+"F17.boolean.opBoolean","MERGE",EDGE,{"derivedFrom":[makeQuery(id+"F16.boolean.opBoolean","MERGE",EDGE,{"derivedFrom":[makeQuery(id+"F11.opExtrude","CAP_EDGE",EDGE,{"disambiguationData":[OSD([subQ1])],"isStart":true}),makeQuery(id+"F16.opExtrude","SWEPT_EDGE",EDGE,{"disambiguationData":[OSD([subQ1,subQ2]),TDD([makeQuery(id+"F15.imprint","INTERSECT",VERTEX,{"derivedFrom":[makeQuery(id+"F11.opExtrude","CAP_EDGE",EDGE,{"disambiguationData":[OSD([subQ2])],"isStart":true}),makeQuery(id+"F13.boolean.opBoolean","MERGE",EDGE,{"derivedFrom":[makeQuery(id+"F11.opExtrude","SWEPT_EDGE",EDGE,{"disambiguationData":[OSD([subQ1,subQ2])]}),makeQuery(id+"F13.opExtrude","SWEPT_EDGE",EDGE,{"disambiguationData":[OSD([subQ1,subQ2])]})]})]})])]})]}),makeQuery(id+"F17.opExtrude","SWEPT_EDGE",EDGE,{"disambiguationData":[OSD([subQ1,subQ0]),TDD([makeQuery(id+"F14.imprint","INTERSECT",VERTEX,{"derivedFrom":[makeQuery(id+"F11.opExtrude","CAP_EDGE",EDGE,{"disambiguationData":[OSD([subQ0])],"isStart":true}),makeQuery(id+"F13.boolean.opBoolean","MERGE",EDGE,{"derivedFrom":[makeQuery(id+"F11.opExtrude","SWEPT_EDGE",EDGE,{"disambiguationData":[OSD([subQ1,subQ0])]}),makeQuery(id+"F13.opExtrude","SWEPT_EDGE",EDGE,{"disambiguationData":[OSD([subQ1,subQ0])]})]})]})])]})]});Q17=makeQuery(id+"F21.opExtrude","CAP_EDGE",EDGE,{"disambiguationData":[OSD([subQ1,subQ0,subQ2]),TDD([makeQuery(id+"F18.imprint","IMPRINT",EDGE,{"disambiguationData":[TD([[makeQuery(id+"F18.imprint","INTERSECT",VERTEX,{"derivedFrom":[subQ3,sQuery(id+"F18.wireOp",EDGE,"E16")]}),-1.0]])],"derivedFrom":subQ3})])],"isStart":false});}
            var Q18;
            {var subQ0=sQuery(id+"F10.wireOp",EDGE,"E9.left");var subQ1=sQuery(id+"F10.wireOp",EDGE,"E9.top");var subQ2=makeQuery(id+"F11.opExtrude","CAP_EDGE",EDGE,{"disambiguationData":[OSD([subQ0])],"isStart":false});var subQ3=makeQuery(id+"F11.opExtrude","CAP_EDGE",EDGE,{"disambiguationData":[OSD([subQ1])],"isStart":false});var subQ5=sQuery(id+"F10.wireOp",EDGE,"E9.right");var subQ6=makeQuery(id+"F11.opExtrude","CAP_EDGE",EDGE,{"disambiguationData":[OSD([subQ5])],"isStart":false});var subQ7=makeQuery(id+"F17.boolean.opBoolean","MERGE",EDGE,{"derivedFrom":[makeQuery(id+"F16.boolean.opBoolean","MERGE",EDGE,{"derivedFrom":[makeQuery(id+"F13.opExtrude","CAP_EDGE",EDGE,{"disambiguationData":[OSD([subQ1])],"isStart":false}),makeQuery(id+"F16.opExtrude","SWEPT_EDGE",EDGE,{"disambiguationData":[OSD([subQ1,subQ5]),TDD([makeQuery(id+"F15.imprint","INTERSECT",VERTEX,{"derivedFrom":[makeQuery(id+"F13.opExtrude","CAP_EDGE",EDGE,{"disambiguationData":[OSD([subQ5]),TDD([makeQuery(id+"F12.imprint","IMPRINT",EDGE,{"disambiguationData":[TD([[makeQuery(id+"F12.imprint","INTERSECT",VERTEX,{"derivedFrom":[subQ3,subQ6]}),1.0]])],"derivedFrom":subQ6})])],"isStart":false}),makeQuery(id+"F13.boolean.opBoolean","MERGE",EDGE,{"derivedFrom":[makeQuery(id+"F11.opExtrude","SWEPT_EDGE",EDGE,{"disambiguationData":[OSD([subQ1,subQ5])]}),makeQuery(id+"F13.opExtrude","SWEPT_EDGE",EDGE,{"disambiguationData":[OSD([subQ1,subQ5])]})]})]})])]})]}),makeQuery(id+"F17.opExtrude","SWEPT_EDGE",EDGE,{"disambiguationData":[OSD([subQ1,subQ0]),TDD([makeQuery(id+"F14.imprint","INTERSECT",VERTEX,{"derivedFrom":[makeQuery(id+"F13.opExtrude","CAP_EDGE",EDGE,{"disambiguationData":[OSD([subQ0]),TDD([makeQuery(id+"F12.imprint","IMPRINT",EDGE,{"disambiguationData":[TD([[makeQuery(id+"F12.imprint","INTERSECT",VERTEX,{"derivedFrom":[subQ3,subQ2]}),1.0]])],"derivedFrom":subQ2})])],"isStart":false}),makeQuery(id+"F13.boolean.opBoolean","MERGE",EDGE,{"derivedFrom":[makeQuery(id+"F11.opExtrude","SWEPT_EDGE",EDGE,{"disambiguationData":[OSD([subQ1,subQ0])]}),makeQuery(id+"F13.opExtrude","SWEPT_EDGE",EDGE,{"disambiguationData":[OSD([subQ1,subQ0])]})]})]})])]})]});Q18=makeQuery(id+"F20.opExtrude","CAP_EDGE",EDGE,{"disambiguationData":[OSD([subQ1,subQ0,subQ5]),TDD([makeQuery(id+"F19.imprint","IMPRINT",EDGE,{"disambiguationData":[TD([[makeQuery(id+"F19.imprint","INTERSECT",VERTEX,{"derivedFrom":[subQ7,sQuery(id+"F19.wireOp",EDGE,"E18")]}),1.0]])],"derivedFrom":subQ7})])],"isStart":false});}
            var Q19;
            {var subQ0=sQuery(id+"F10.wireOp",EDGE,"E9.left");var subQ1=sQuery(id+"F10.wireOp",EDGE,"E9.top");var subQ2=makeQuery(id+"F11.opExtrude","CAP_EDGE",EDGE,{"disambiguationData":[OSD([subQ0])],"isStart":false});var subQ3=makeQuery(id+"F11.opExtrude","CAP_EDGE",EDGE,{"disambiguationData":[OSD([subQ1])],"isStart":false});var subQ5=sQuery(id+"F10.wireOp",EDGE,"E9.right");var subQ6=makeQuery(id+"F11.opExtrude","CAP_EDGE",EDGE,{"disambiguationData":[OSD([subQ5])],"isStart":false});var subQ7=makeQuery(id+"F17.boolean.opBoolean","MERGE",EDGE,{"derivedFrom":[makeQuery(id+"F16.boolean.opBoolean","MERGE",EDGE,{"derivedFrom":[makeQuery(id+"F13.opExtrude","CAP_EDGE",EDGE,{"disambiguationData":[OSD([subQ1])],"isStart":false}),makeQuery(id+"F16.opExtrude","SWEPT_EDGE",EDGE,{"disambiguationData":[OSD([subQ1,subQ5]),TDD([makeQuery(id+"F15.imprint","INTERSECT",VERTEX,{"derivedFrom":[makeQuery(id+"F13.opExtrude","CAP_EDGE",EDGE,{"disambiguationData":[OSD([subQ5]),TDD([makeQuery(id+"F12.imprint","IMPRINT",EDGE,{"disambiguationData":[TD([[makeQuery(id+"F12.imprint","INTERSECT",VERTEX,{"derivedFrom":[subQ3,subQ6]}),1.0]])],"derivedFrom":subQ6})])],"isStart":false}),makeQuery(id+"F13.boolean.opBoolean","MERGE",EDGE,{"derivedFrom":[makeQuery(id+"F11.opExtrude","SWEPT_EDGE",EDGE,{"disambiguationData":[OSD([subQ1,subQ5])]}),makeQuery(id+"F13.opExtrude","SWEPT_EDGE",EDGE,{"disambiguationData":[OSD([subQ1,subQ5])]})]})]})])]})]}),makeQuery(id+"F17.opExtrude","SWEPT_EDGE",EDGE,{"disambiguationData":[OSD([subQ1,subQ0]),TDD([makeQuery(id+"F14.imprint","INTERSECT",VERTEX,{"derivedFrom":[makeQuery(id+"F13.opExtrude","CAP_EDGE",EDGE,{"disambiguationData":[OSD([subQ0]),TDD([makeQuery(id+"F12.imprint","IMPRINT",EDGE,{"disambiguationData":[TD([[makeQuery(id+"F12.imprint","INTERSECT",VERTEX,{"derivedFrom":[subQ3,subQ2]}),1.0]])],"derivedFrom":subQ2})])],"isStart":false}),makeQuery(id+"F13.boolean.opBoolean","MERGE",EDGE,{"derivedFrom":[makeQuery(id+"F11.opExtrude","SWEPT_EDGE",EDGE,{"disambiguationData":[OSD([subQ1,subQ0])]}),makeQuery(id+"F13.opExtrude","SWEPT_EDGE",EDGE,{"disambiguationData":[OSD([subQ1,subQ0])]})]})]})])]})]});Q19=makeQuery(id+"F20.opExtrude","CAP_EDGE",EDGE,{"disambiguationData":[OSD([subQ1,subQ0,subQ5]),TDD([makeQuery(id+"F19.imprint","IMPRINT",EDGE,{"disambiguationData":[TD([[makeQuery(id+"F19.imprint","INTERSECT",VERTEX,{"derivedFrom":[subQ7,sQuery(id+"F19.wireOp",EDGE,"E19")]}),-1.0]])],"derivedFrom":subQ7})])],"isStart":false});}
            var Q20;
            {var subQ0=sQuery(id+"F10.wireOp",EDGE,"E9.left");var subQ1=sQuery(id+"F10.wireOp",EDGE,"E9.top");var subQ2=sQuery(id+"F10.wireOp",EDGE,"E9.right");var subQ3=makeQuery(id+"F17.boolean.opBoolean","MERGE",EDGE,{"derivedFrom":[makeQuery(id+"F16.boolean.opBoolean","MERGE",EDGE,{"derivedFrom":[makeQuery(id+"F11.opExtrude","CAP_EDGE",EDGE,{"disambiguationData":[OSD([subQ1])],"isStart":true}),makeQuery(id+"F16.opExtrude","SWEPT_EDGE",EDGE,{"disambiguationData":[OSD([subQ1,subQ2]),TDD([makeQuery(id+"F15.imprint","INTERSECT",VERTEX,{"derivedFrom":[makeQuery(id+"F11.opExtrude","CAP_EDGE",EDGE,{"disambiguationData":[OSD([subQ2])],"isStart":true}),makeQuery(id+"F13.boolean.opBoolean","MERGE",EDGE,{"derivedFrom":[makeQuery(id+"F11.opExtrude","SWEPT_EDGE",EDGE,{"disambiguationData":[OSD([subQ1,subQ2])]}),makeQuery(id+"F13.opExtrude","SWEPT_EDGE",EDGE,{"disambiguationData":[OSD([subQ1,subQ2])]})]})]})])]})]}),makeQuery(id+"F17.opExtrude","SWEPT_EDGE",EDGE,{"disambiguationData":[OSD([subQ1,subQ0]),TDD([makeQuery(id+"F14.imprint","INTERSECT",VERTEX,{"derivedFrom":[makeQuery(id+"F11.opExtrude","CAP_EDGE",EDGE,{"disambiguationData":[OSD([subQ0])],"isStart":true}),makeQuery(id+"F13.boolean.opBoolean","MERGE",EDGE,{"derivedFrom":[makeQuery(id+"F11.opExtrude","SWEPT_EDGE",EDGE,{"disambiguationData":[OSD([subQ1,subQ0])]}),makeQuery(id+"F13.opExtrude","SWEPT_EDGE",EDGE,{"disambiguationData":[OSD([subQ1,subQ0])]})]})]})])]})]});Q20=makeQuery(id+"F20.opExtrude","CAP_EDGE",EDGE,{"disambiguationData":[OSD([subQ1,subQ0,subQ2]),TDD([makeQuery(id+"F19.imprint","IMPRINT",EDGE,{"disambiguationData":[TD([[makeQuery(id+"F19.imprint","INTERSECT",VERTEX,{"derivedFrom":[subQ3,sQuery(id+"F19.wireOp",EDGE,"E18")]}),1.0]])],"derivedFrom":subQ3})])],"isStart":false});}
            chamfer(context, id + "F29", {"entities" : qUnion([Q0, Q1, Q2, Q3, Q4, Q5, Q6, Q7, Q8, Q9, Q10, Q11, Q12, Q13, Q14, Q15, Q16, Q17, Q18, Q19, Q20]), "width" : 2 * mm, "tangentPropagation" : true});
        }
        {
            var Q0;
            Q0=makeQuery(id+"F1.opExtrude","SWEPT_BODY",BODY,{"disambiguationData":[OSD([sQuery(id+"F0.wireOp",EDGE,"E1.bottom"),sQuery(id+"F0.wireOp",EDGE,"E1.top"),sQuery(id+"F0.wireOp",EDGE,"E1.left"),sQuery(id+"F0.wireOp",EDGE,"E1.right")])]});
            deleteBodies(context, id + "F30", {"entities" : qUnion([Q0])});
        }
    });
